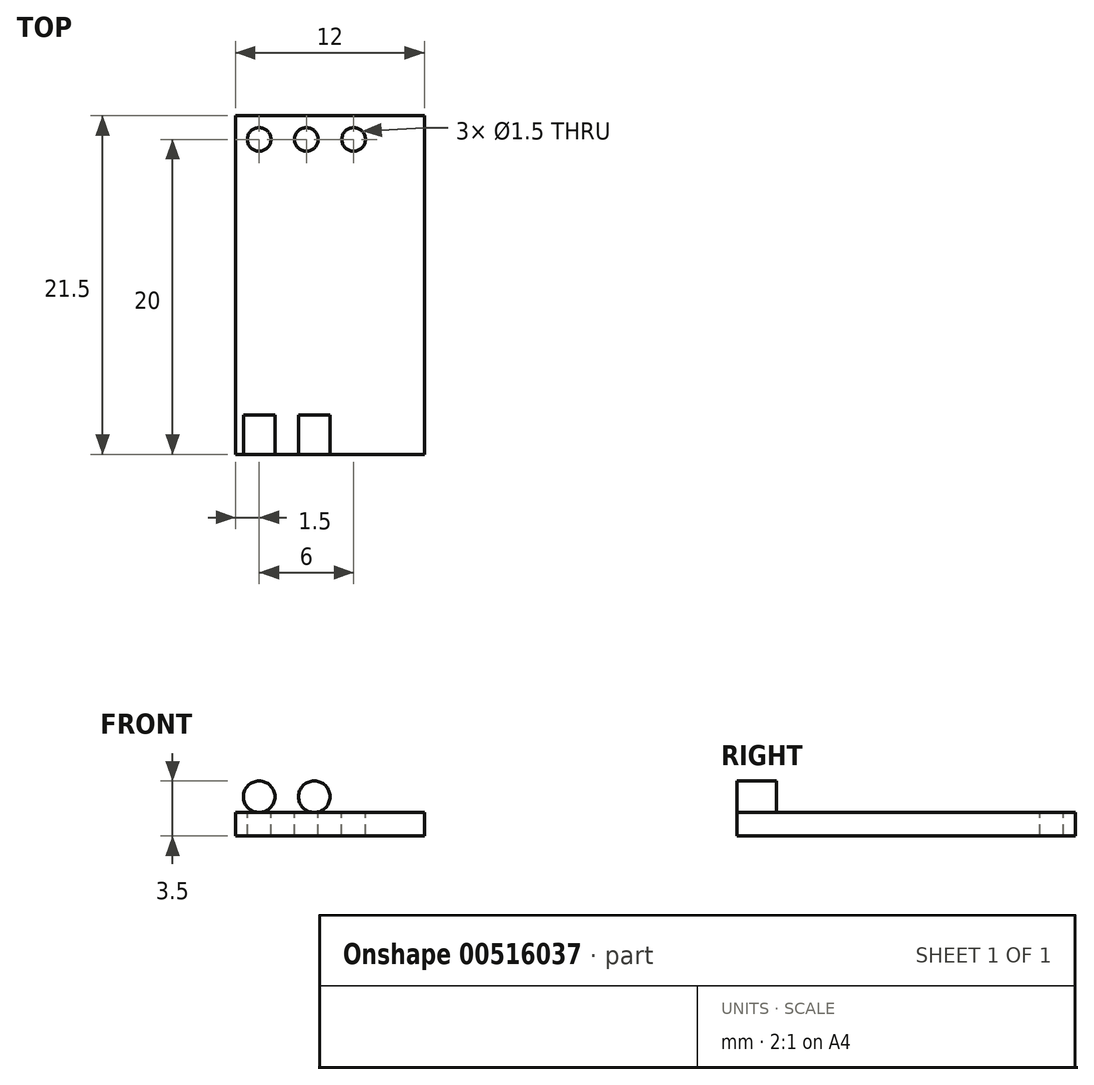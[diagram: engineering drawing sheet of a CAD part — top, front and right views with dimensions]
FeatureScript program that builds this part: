
annotation { "Feature Type Name" : "Feature", "Feature Type Description" : "" }
export const myFeature = defineFeature(function(context is Context, id is Id, definition is map)
    precondition{}
    {
        {
            var Q0;
            Q0=qCreatedBy(makeId("Top.planeOp"),FACE);
            var sketch = newSketch(context, id + "F0", { "sketchPlane" : qUnion([Q0])});
            skLineSegment(sketch, "E0.bottom", {"start": v(-6, -10.75) * mm, "end": v(6, -10.75) * mm});
            skLineSegment(sketch, "E0.top", {"start": v(-6, 10.75) * mm, "end": v(6, 10.75) * mm});
            skLineSegment(sketch, "E0.left", {"start": v(-6, -10.75) * mm, "end": v(-6, 10.75) * mm});
            skLineSegment(sketch, "E0.right", {"start": v(6, -10.75) * mm, "end": v(6, 10.75) * mm});
            skSolve(sketch);
        }
        {
            var Q0;
            Q0 = qSketchRegion(id + "F0", true);
            extrude(context, id + "F1", {"entities" : qUnion([Q0]), "depth" : 1.5 * mm, "offsetDistance" : 25 * mm});
        }
        {
            var Q0;
            Q0=makeQuery(id+"F1.opExtrude","SWEPT_FACE",FACE,{"disambiguationData":[OSD([sQuery(id+"F0.wireOp",EDGE,"E0.bottom")])]});
            cPlane(context, id + "F2", {"entities" : qUnion([Q0]), "cplaneType" : CPlaneType.OFFSET, "offset" : 2.5 * mm, "oppositeDirection" : true, "width" : 150 * mm, "height" : 150 * mm});
        }
        {
            var Q0;
            Q0=qCreatedBy(id+"F2.planeOp",FACE);
            var sketch = newSketch(context, id + "F3", { "sketchPlane" : qUnion([Q0])});
            skCircle(sketch, "E1", {"center": v(-4.5, 2.5) * mm, "radius": 1 * mm});
            skCircle(sketch, "E2", {"center": v(-1, 2.5) * mm, "radius": 1 * mm});
            skSolve(sketch);
        }
        {
            var Q0;
            Q0 = qSketchRegion(id + "F3", true);
            var Q1;
            Q1=makeQuery(id+"F1.opExtrude","SWEPT_FACE",FACE,{"disambiguationData":[OSD([sQuery(id+"F0.wireOp",EDGE,"E0.bottom")])]});
            extrude(context, id + "F4", {"entities" : qUnion([Q0]), "operationType" : NewBodyOperationType.ADD, "endBound" : BoundingType.UP_TO_SURFACE, "depth" : 25 * mm, "endBoundEntityFace" : qUnion([Q1]), "offsetDistance" : 25 * mm});
        }
        {
            var Q0;
            Q0=makeQuery(id+"F1.opExtrude","CAP_FACE",FACE,{"disambiguationData":[OSD([sQuery(id+"F0.wireOp",EDGE,"E0.bottom"),sQuery(id+"F0.wireOp",EDGE,"E0.top"),sQuery(id+"F0.wireOp",EDGE,"E0.left"),sQuery(id+"F0.wireOp",EDGE,"E0.right")])],"isStart":false});
            var sketch = newSketch(context, id + "F5", { "sketchPlane" : qUnion([Q0])});
            skCircle(sketch, "E3", {"center": v(-4.5, 9.25) * mm, "radius": 0.75 * mm});
            skCircle(sketch, "E4", {"center": v(-1.5, 9.25) * mm, "radius": 0.75 * mm});
            skCircle(sketch, "E5", {"center": v(1.5, 9.25) * mm, "radius": 0.75 * mm});
            skLineSegment(sketch, "E6", {"start": v(-4.5, 9.25) * mm, "end": v(1.5, 9.25) * mm, "construction": true});
            skSolve(sketch);
        }
        {
            var Q0;
            Q0 = qSketchRegion(id + "F5", true);
            extrude(context, id + "F6", {"entities" : qUnion([Q0]), "operationType" : NewBodyOperationType.REMOVE, "endBound" : BoundingType.THROUGH_ALL, "oppositeDirection" : true, "depth" : 25 * mm, "offsetDistance" : 25 * mm});
        }
    });
